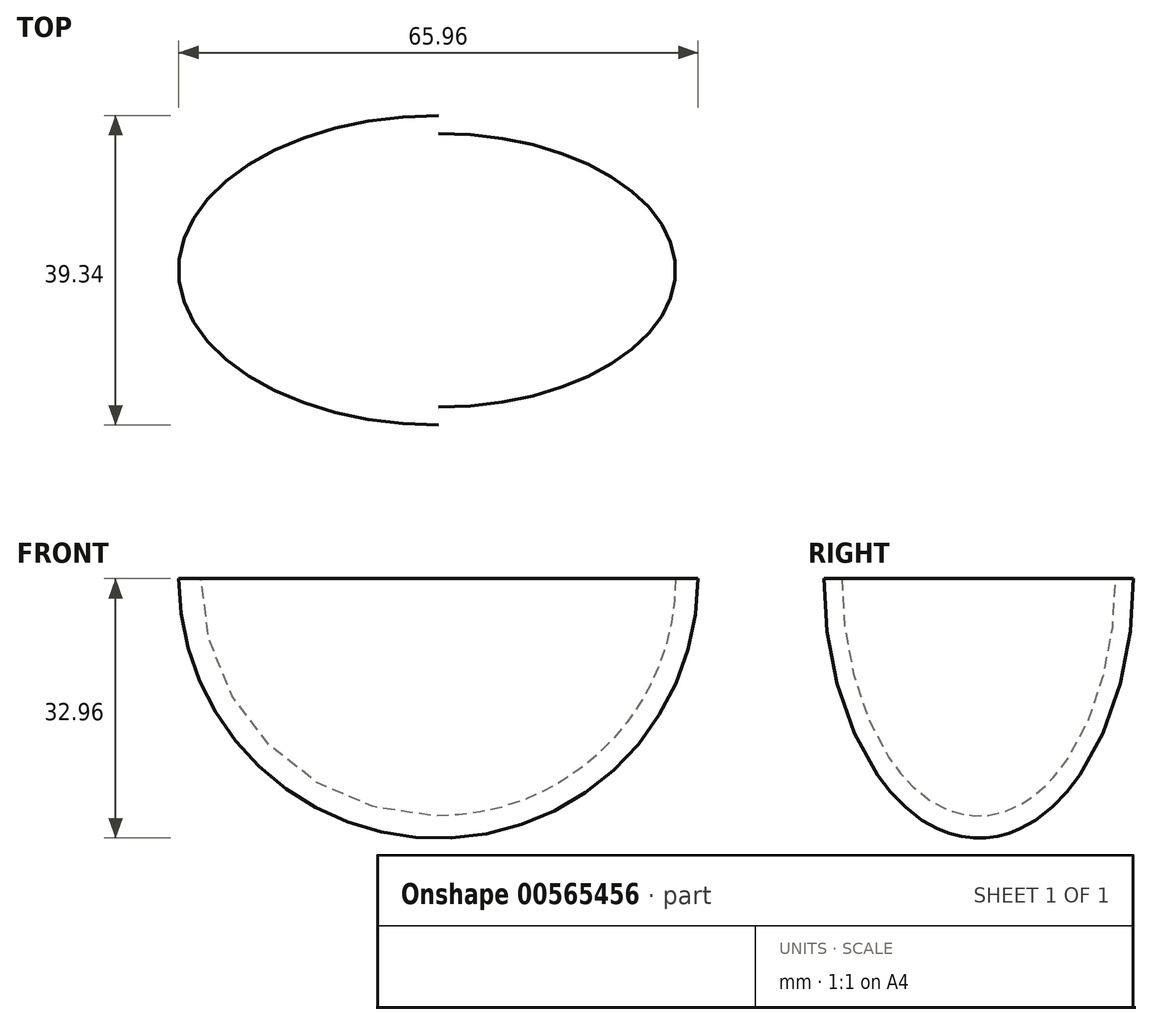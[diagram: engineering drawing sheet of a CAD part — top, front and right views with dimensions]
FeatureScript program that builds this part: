
annotation { "Feature Type Name" : "Feature", "Feature Type Description" : "" }
export const myFeature = defineFeature(function(context is Context, id is Id, definition is map)
    precondition{}
    {
        {
            var Q0;
            Q0=qCreatedBy(makeId("Top.planeOp"),FACE);
            var sketch = newSketch(context, id + "F0", { "sketchPlane" : qUnion([Q0])});
            skEllipticalArc(sketch, "E0", {});
            skLineSegment(sketch, "E1", {"start": v(-62.2, 25.31) * mm, "end": v(-62.2, -14.03) * mm});
            const initialGuessF0  = {"E0": [-0.06219679152173127, 0.005641103905604755, 1, 0, 0.03297876559153266, 0.0196723, 4.71238898038469, 1.5707963267948966]};
            skSetInitialGuess(sketch, initialGuessF0);
            skSolve(sketch);
        }
        {
            var Q0;
            Q0=makeQuery(id+"F0.imprint","IMPRINT",FACE,{"disambiguationData":[TD([[makeQuery(id+"F0.imprint","IMPRINT",EDGE,{"derivedFrom":sQuery(id+"F0.wireOp",EDGE,"E0")}),1.0]])]});
            var Q1;
            Q1=sQuery(id+"F0.wireOp",EDGE,"E1");
            revolve(context, id + "F1", {"entities" : qUnion([Q0]), "axis" : qUnion([Q1]), "revolveType" : RevolveType.ONE_DIRECTION, "oppositeDirection" : true, "angle" : 180 * degree});
        }
        {
            var Q0;
            Q0=makeQuery(id+"F1.opRevolve","CAP_FACE",FACE,{"disambiguationData":[OSD([sQuery(id+"F0.wireOp",EDGE,"E0"),sQuery(id+"F0.wireOp",EDGE,"E1")])],"isStart":false});
            var sketch = newSketch(context, id + "F2", { "sketchPlane" : qUnion([Q0])});
            skEllipticalArc(sketch, "E2", {});
            skLineSegment(sketch, "E3", {"start": v(-62.2, 23.03) * mm, "end": v(-62.2, -11.75) * mm});
            const initialGuessF2  = {"E2": [-0.06219679152173128, 0.005641103905604756, 1, 0, 0.03013838117522325, 0.0173863, 4.71238898038469, 1.5707963267948966]};
            skSetInitialGuess(sketch, initialGuessF2);
            skSolve(sketch);
        }
        {
            var Q0;
            Q0=makeQuery(id+"F2.imprint","IMPRINT",FACE,{"disambiguationData":[TD([[makeQuery(id+"F2.imprint","IMPRINT",EDGE,{"derivedFrom":sQuery(id+"F2.wireOp",EDGE,"E2")}),1.0]])]});
            var Q1;
            Q1=sQuery(id+"F2.wireOp",EDGE,"E2");
            var Q2;
            Q2=sQuery(id+"F2.wireOp",EDGE,"E3");
            revolve(context, id + "F3", {"operationType" : NewBodyOperationType.REMOVE, "entities" : qUnion([Q0]), "surfaceEntities" : qUnion([Q1]), "axis" : qUnion([Q2]), "revolveType" : RevolveType.ONE_DIRECTION, "oppositeDirection" : true, "angle" : 180 * degree});
        }
    });
